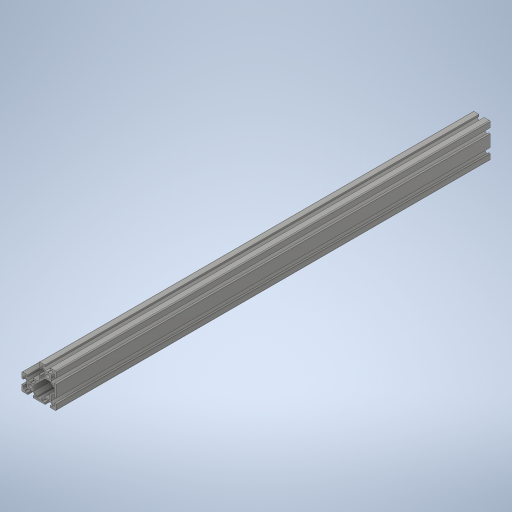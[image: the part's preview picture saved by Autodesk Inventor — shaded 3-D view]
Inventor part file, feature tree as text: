
AUTODESK INVENTOR PART (.ipt)
format: ipt  version: 2024 (Build 280153000, 153)  size: 448,000 bytes
history: native  units: mm
features: thread x4, sketch x3, hole x2, extrude x1
ambient origin geometry x8: Origin, YZ Plane, XZ Plane, XY Plane, X Axis, Y Axis, Z Axis, Center Point
bodies: Solid1 (feature_tree)
feature tree (10):
  extrude  "Extrusion1"  Depth=10.0mm TaperAngle=0.0deg
  hole  "Hole1"  [1 undecoded]
  hole  "Hole2"  [1 undecoded]
  thread  "Thread1"  [1 undecoded]
  thread  "Thread2"  [1 undecoded]
  thread  "Thread3"  [1 undecoded]
  thread  "Thread4"  [1 undecoded]
  sketch  "Sketch_1"  dims[d0=505.0mm d1=0.0mm]
  sketch  "Sketch2"  dims[d2=4.2mm d3=6.0mm d4=4.0mm d5=2.0mm d6=90.0deg d7=425.0mm d8=0.0mm]
  sketch  "Sketch3"  dims[d9=4.2mm d10=6.0mm d11=4.0mm d12=2.0mm d13=90.0deg d14=425.0mm d15=0.0mm d16=10.0mm d17=0.0mm d18=10.0mm d19=0.0mm d20=10.0mm d21=0.0mm d22=10.0mm d23=0.0mm d24=0.5mm d25=0.872665mm d26=0.5mm d27=0.872665mm]
note: 6 required parameter values undecoded (feature->parameter linkage not recoverable at this tier; creation-order binding heuristic only, values carry confidence <= 0.55)
